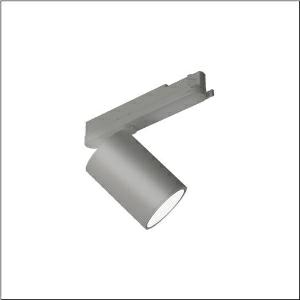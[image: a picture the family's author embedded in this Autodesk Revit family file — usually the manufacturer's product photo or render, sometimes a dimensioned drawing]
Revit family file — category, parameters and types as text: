
# Revit family: spot_31_51sf64mad4b
name_source: partatom
category: Lighting Fixtures
units: mm (PartAtom-declared; Revit-internal decimal feet)

## family parameters
Cut with Voids When Loaded = No
Host = Face
Light Source = No
Part Type = Normal
Room Calculation Point = No
Round Connector Dimension = Use Diameter
Shared = No

## types (1)
- --- (1 x LED, 5250 lm, 41.4 W, 4000K)
    Apparent Load = 41 VA
    CIE Flux Codes = 93 97 100 100 100
    Color Rendering = 90
    Color Temperature = 4000K
    Default Elevation = 1800 mm
    Description = Spot 31, directional spotlight, light control with lens, of PMMA, LED rated luminous flux: 5.040lm, light colour: 940, control gear: ECG Multilumen, with 3-phase adapter, mains connection: 220..240V, AC, 50/60Hz, of aluminium, metallic grey (RAL 9006), length: 213mm, diameter: 90mm, protection rating (complete): IP20, insulation class (complete): insulation class I (protective earthing), certification: CE, impact resistance: IK02, permissible ambient temperature for indoor applications: -20..+40°C, packaging unit: 1 piece
    Height = 175 mm
    Lamp = 1 x LED
    Lamp Light Flux = 5250 lm
    Lamp Power = 41.4 W
    Lamp count = 1
    Length = 90 mm
    Luminous efficacy = 127 lm/W
    Manufacturer = Siteco
    ModVariant = No
    Model = 51SF64MAD4B
    Mounting Place = Ceiling
    Mounting Type = Pendant
    Number of Poles = 1
    OnlyDefault = Yes
    Power Factor = 1
    Product Name = Spot 31
    Product group = directional spotlight
    ProductGroupID = 905
    Protection Class = Protection class I
    Protection Degree = IP 20
    RLX_Detail_Level = 1
    RLX_Emergency_Light_Flux = 0 lm
    RLX_Emergency_Type = 0
    RLX_Emergency_Type_DB = No
    RlxData = <blob elided: 20069 chars, md5=931ea0c0>
    Socket = socket
    Standby Power = 0 W
    System Light Flux = 5250 lm
    System Power = 41 W
    Type Comments = factory setting: luminous flux: 100 % | (ON | ON | ON | ON) | 1050 mA
    Type Image = l_1273725.jpg
    URL = http://relux.com
    VarID = @adj_095827
    Voltage = 0 V
    Weight = 0.00 kg
    Width = 0 mm  [stored 0 ft]

note: [stored X ft] marks values corroborated as IEEE doubles in the binary element streams (Revit-internal decimal feet)

## geometry (parser evidence)
native form markers: Blend x4, Sweep x11
no freeform markers — native parametric forms only
